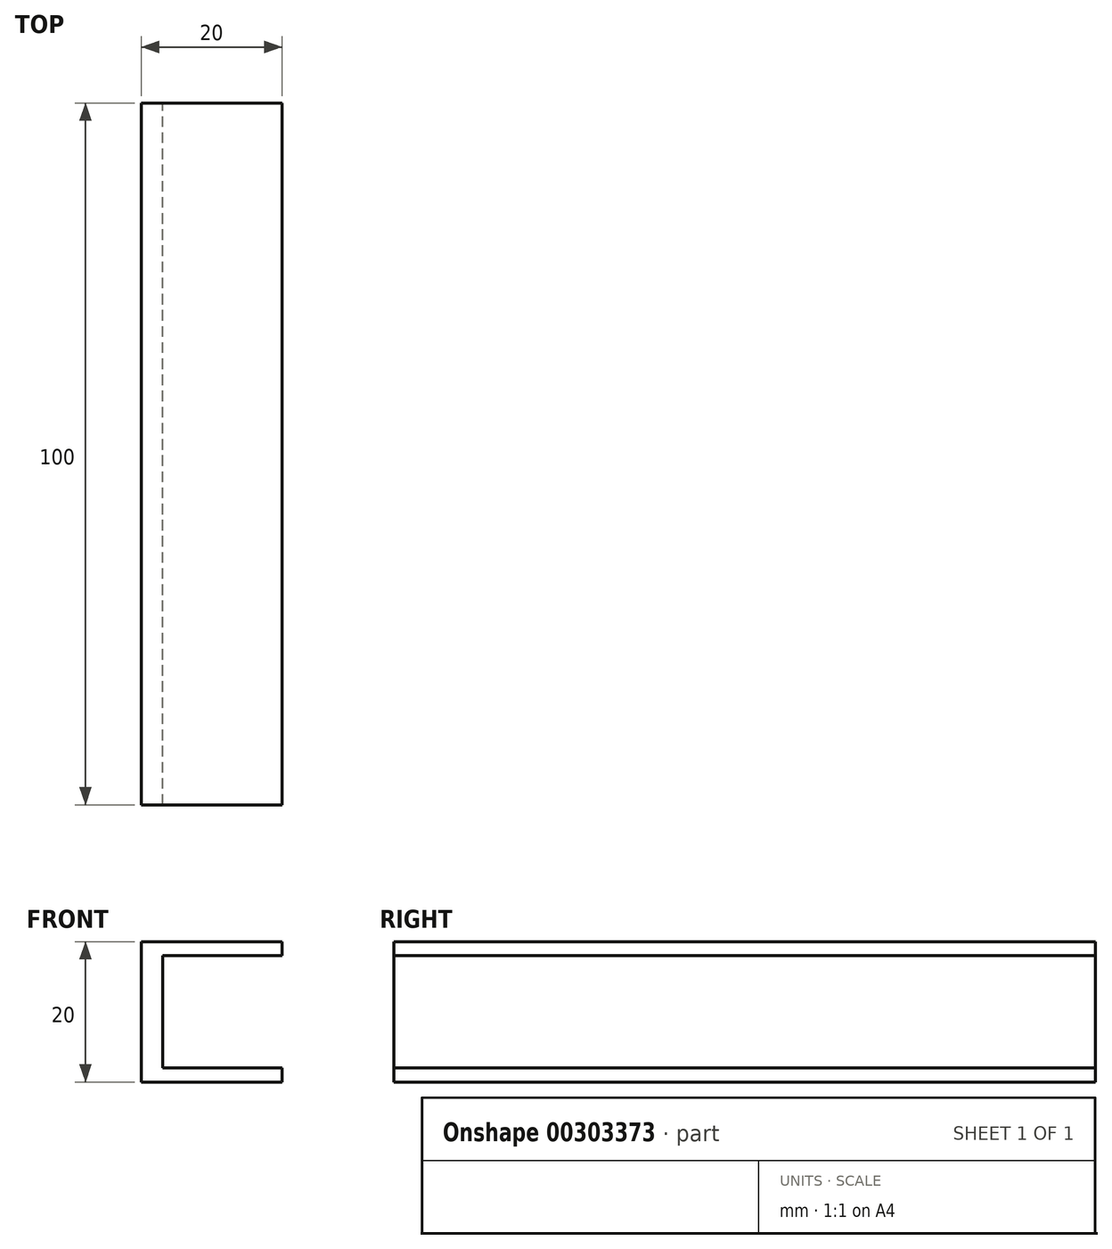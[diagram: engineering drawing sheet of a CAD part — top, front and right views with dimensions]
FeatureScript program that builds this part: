
annotation { "Feature Type Name" : "Feature", "Feature Type Description" : "" }
export const myFeature = defineFeature(function(context is Context, id is Id, definition is map)
    precondition{}
    {
        {
            var Q0;
            Q0=qCreatedBy(makeId("Front.planeOp"),FACE);
            var sketch = newSketch(context, id + "F0", { "sketchPlane" : qUnion([Q0])});
            skLineSegment(sketch, "E0.bottom", {"start": v(10, 10) * mm, "end": v(-10, 10) * mm});
            skLineSegment(sketch, "E0.top", {"start": v(10, -10) * mm, "end": v(-10, -10) * mm});
            skLineSegment(sketch, "E0.left", {"start": v(10, 10) * mm, "end": v(10, 8) * mm});
            skLineSegment(sketch, "E0.right", {"start": v(-10, 10) * mm, "end": v(-10, -10) * mm});
            skPoint(sketch, "E0.middle", {"position": v(0, 0) * mm});
            skLineSegment(sketch, "E1", {"start": v(10, 8) * mm, "end": v(-7, 8) * mm});
            skLineSegment(sketch, "E2", {"start": v(-7, 8) * mm, "end": v(-7, -8) * mm});
            skLineSegment(sketch, "E3", {"start": v(-7, -8) * mm, "end": v(10, -8) * mm});
            skLineSegment(sketch, "E4.trimOffspring", {"start": v(10, -8) * mm, "end": v(10, -10) * mm});
            skSolve(sketch);
        }
        {
            var Q0;
            Q0=qSketchRegion(id+"F0",true);
            extrude(context, id + "F1", {"entities" : qUnion([Q0]), "depth" : 100 * mm});
        }
    });
